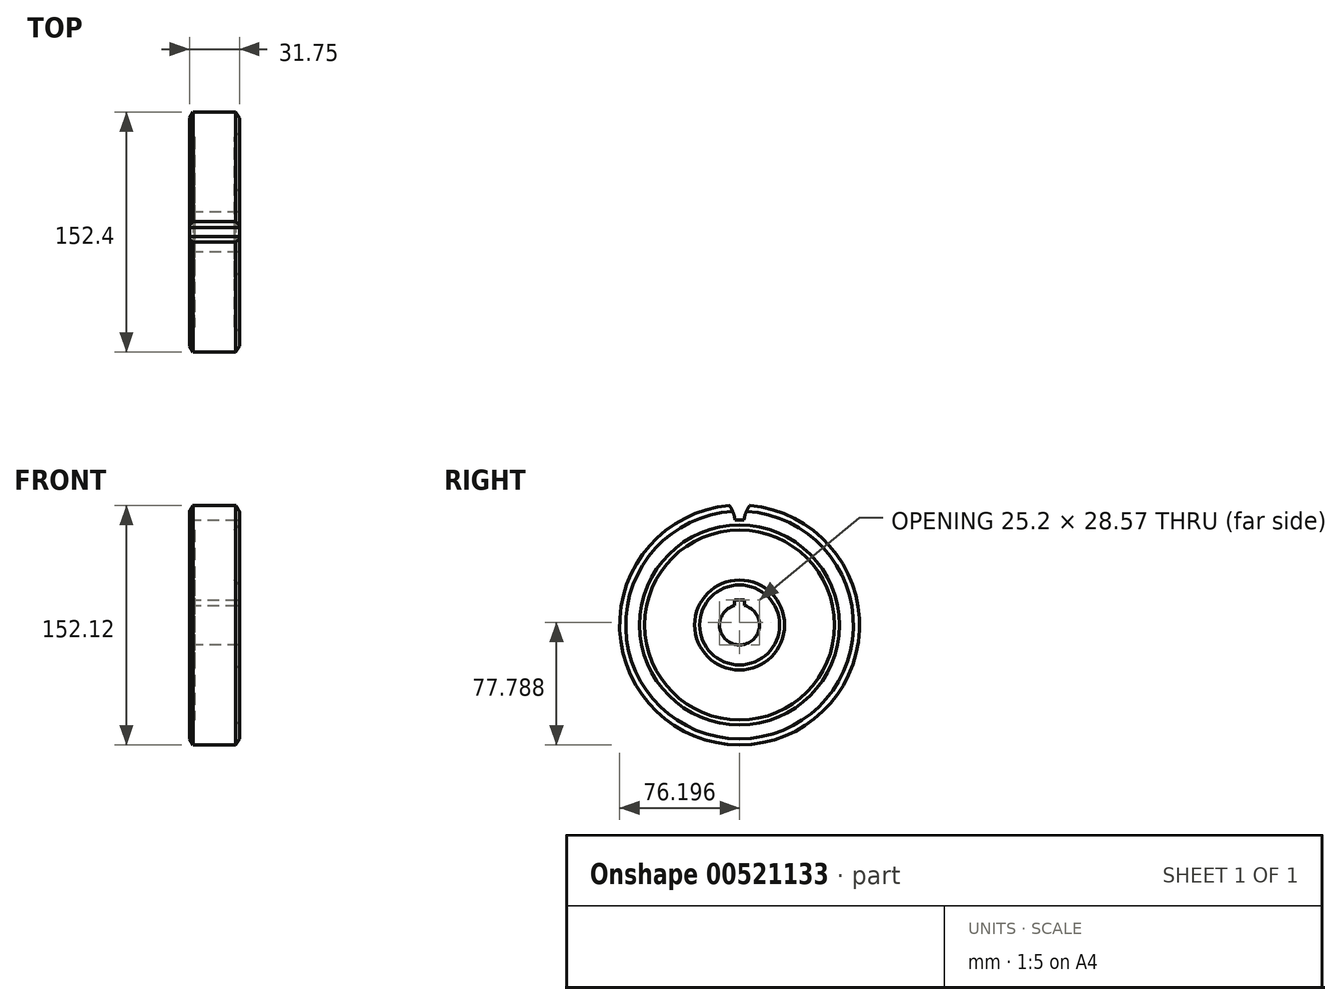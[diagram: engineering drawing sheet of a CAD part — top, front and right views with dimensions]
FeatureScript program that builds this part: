
annotation { "Feature Type Name" : "Feature", "Feature Type Description" : "" }
export const myFeature = defineFeature(function(context is Context, id is Id, definition is map)
    precondition{}
    {
        {
            var Q0;
            Q0=qCreatedBy(makeId("Top.planeOp"),FACE);
            var sketch = newSketch(context, id + "F0", { "sketchPlane" : qUnion([Q0])});
            skLineSegment(sketch, "E0", {"start": v(39.2, 14.55) * mm, "end": v(25.57, 14.55) * mm});
            skLineSegment(sketch, "E1", {"start": v(25.57, 14.55) * mm, "end": v(23.33, 10.66) * mm});
            skLineSegment(sketch, "E2", {"start": v(23.33, 10.66) * mm, "end": v(23.33, 1.85) * mm});
            skLineSegment(sketch, "E3", {"start": v(23.33, 1.85) * mm, "end": v(26.5, -1.33) * mm});
            skLineSegment(sketch, "E4", {"start": v(26.5, -1.33) * mm, "end": v(26.5, -33.08) * mm});
            skLineSegment(sketch, "E5", {"start": v(26.5, -33.08) * mm, "end": v(23.33, -36.25) * mm});
            skLineSegment(sketch, "E6", {"start": v(23.33, -36.25) * mm, "end": v(23.33, -48.95) * mm});
            skLineSegment(sketch, "E7", {"start": v(23.33, -48.95) * mm, "end": v(39.2, -48.95) * mm});
            skLineSegment(sketch, "E8", {"start": v(39.2, 14.55) * mm, "end": v(39.2, -61.65) * mm});
            skLineSegment(sketch, "E9", {"start": v(39.2, -61.65) * mm, "end": v(81.28, -61.65) * mm});
            skLineSegment(sketch, "E10.MirrorCS", {"start": v(52.83, 14.55) * mm, "end": v(55.08, 10.66) * mm});
            skLineSegment(sketch, "E11.MirrorCS", {"start": v(39.2, 14.55) * mm, "end": v(52.83, 14.55) * mm});
            skLineSegment(sketch, "E12.MirrorCS", {"start": v(55.08, 1.85) * mm, "end": v(51.9, -1.33) * mm});
            skLineSegment(sketch, "E13.MirrorCS", {"start": v(51.9, -33.08) * mm, "end": v(55.08, -36.25) * mm});
            skLineSegment(sketch, "E14.MirrorCS", {"start": v(55.08, -48.95) * mm, "end": v(39.2, -48.95) * mm});
            skLineSegment(sketch, "E15.MirrorCS", {"start": v(55.08, -36.25) * mm, "end": v(55.08, -48.95) * mm});
            skLineSegment(sketch, "E16.MirrorCS", {"start": v(55.08, 10.66) * mm, "end": v(55.08, 1.85) * mm});
            skLineSegment(sketch, "E17.MirrorCS", {"start": v(51.9, -1.33) * mm, "end": v(51.9, -33.08) * mm});
            skSolve(sketch);
        }
        {
            var Q0;
            Q0=qSketchRegion(id+"F0",true);
            var Q1;
            Q1=sQuery(id+"F0.wireOp",EDGE,"E9");
            revolve(context, id + "F1", {"entities" : qUnion([Q0]), "axis" : qUnion([Q1]), "revolveType" : RevolveType.FULL});
        }
        {
            var Q0;
            Q0=makeQuery(id+"F1.opRevolve","SWEPT_FACE",FACE,{"disambiguationData":[OSD([sQuery(id+"F0.wireOp",EDGE,"E16.MirrorCS")])]});
            var sketch = newSketch(context, id + "F2", { "sketchPlane" : qUnion([Q0])});
            skArc(sketch, "E18", {"start": v(-64.51, 66.68) * mm, "mid": v(-65.05, 69.48) * mm, "end": v(-66, 72.18) * mm});
            skArc(sketch, "E19.MirrorCS", {"start": v(-58.8, 66.67) * mm, "mid": v(-58.26, 69.48) * mm, "end": v(-57.3, 72.18) * mm});
            skLineSegment(sketch, "E20", {"start": v(-64.51, 66.68) * mm, "end": v(-58.8, 66.68) * mm});
            skPoint(sketch, "E21.start.orphan", {"position": v(-61.65, 63.5) * mm});
            skPoint(sketch, "E22.orphan", {"position": v(-56.88, 73.06) * mm});
            skPoint(sketch, "E23.MirrorCS.end.orphan", {"position": v(-57.62, 69.57) * mm});
            skArc(sketch, "E24.0", {"start": v(-55.11, 75.92) * mm, "mid": v(-61.65, 76.2) * mm, "end": v(-68.2, 75.92) * mm});
            skArc(sketch, "E25", {"start": v(-64.51, 66.68) * mm, "mid": v(-65.74, 71.54) * mm, "end": v(-68.2, 75.92) * mm});
            skArc(sketch, "E26.MirrorCS", {"start": v(-58.8, 66.68) * mm, "mid": v(-57.57, 71.54) * mm, "end": v(-55.11, 75.92) * mm});
            skSolve(sketch);
        }
        {
            var Q0;
            {var subQ0=sQuery(id+"F2.wireOp",EDGE,"E20");Q0=makeQuery(id+"F2.imprint","IMPRINT",FACE,{"disambiguationData":[TD([[makeQuery(id+"F2.imprint","IMPRINT",EDGE,{"derivedFrom":subQ0}),1.0]])]});}
            var Q1;
            {var subQ0=sQuery(id+"F2.wireOp",EDGE,"E24.0");Q1=makeQuery(id+"F2.imprint","IMPRINT",FACE,{"disambiguationData":[TD([[makeQuery(id+"F2.imprint","IMPRINT",EDGE,{"derivedFrom":subQ0}),1.0]])]});}
            extrude(context, id + "F3", {"entities" : qUnion([Q0, Q1]), "operationType" : NewBodyOperationType.REMOVE, "endBound" : BoundingType.THROUGH_ALL, "oppositeDirection" : true, "depth" : 25.4 * mm, "offsetDistance" : 25.4 * mm});
        }
        {
            var Q0;
            Q0=makeQuery(id+"F1.opRevolve","SWEPT_FACE",FACE,{"disambiguationData":[OSD([sQuery(id+"F0.wireOp",EDGE,"E15.MirrorCS")])]});
            var sketch = newSketch(context, id + "F4", { "sketchPlane" : qUnion([Q0])});
            skArc(sketch, "E27.0", {"start": v(-58.48, 12.3) * mm, "mid": v(-61.65, 12.7) * mm, "end": v(-64.83, 12.3) * mm});
            skLineSegment(sketch, "E28", {"start": v(-61.65, 0) * mm, "end": v(-61.65, 12.7) * mm});
            skLineSegment(sketch, "E29", {"start": v(-61.65, 15.88) * mm, "end": v(-64.83, 15.88) * mm});
            skLineSegment(sketch, "E30", {"start": v(-64.83, 15.88) * mm, "end": v(-64.83, 12.3) * mm});
            skLineSegment(sketch, "E31.MirrorCS", {"start": v(-58.48, 15.88) * mm, "end": v(-58.48, 12.3) * mm});
            skLineSegment(sketch, "E32.MirrorCS", {"start": v(-61.65, 15.88) * mm, "end": v(-58.48, 15.88) * mm});
            skSolve(sketch);
        }
        {
            var Q0;
            Q0=qSketchRegion(id+"F4",true);
            extrude(context, id + "F5", {"entities" : qUnion([Q0]), "operationType" : NewBodyOperationType.REMOVE, "endBound" : BoundingType.THROUGH_ALL, "oppositeDirection" : true, "depth" : 25.4 * mm, "offsetDistance" : 25.4 * mm});
        }
    });
